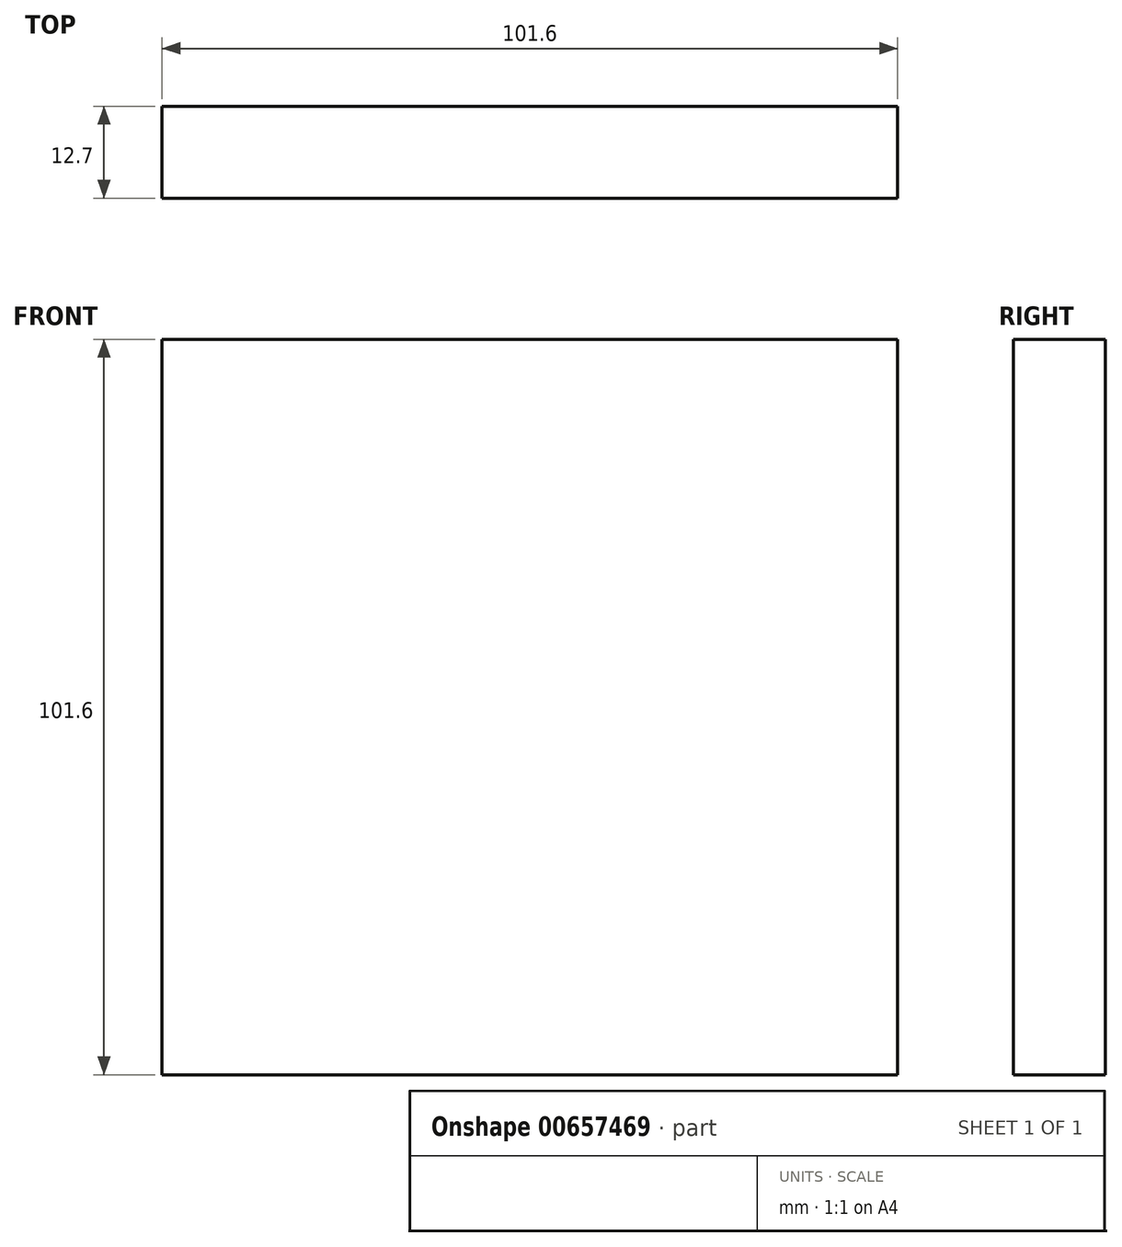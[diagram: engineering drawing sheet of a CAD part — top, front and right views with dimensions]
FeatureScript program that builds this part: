
annotation { "Feature Type Name" : "Feature", "Feature Type Description" : "" }
export const myFeature = defineFeature(function(context is Context, id is Id, definition is map)
    precondition{}
    {
        {
            var Q0;
            Q0=qCreatedBy(makeId("Front.planeOp"),FACE);
            var sketch = newSketch(context, id + "F0", { "sketchPlane" : qUnion([Q0])});
            skLineSegment(sketch, "E0.bottom", {"start": v(-47.38, 52.1) * mm, "end": v(54.22, 52.1) * mm});
            skLineSegment(sketch, "E0.top", {"start": v(-47.38, -49.5) * mm, "end": v(54.22, -49.5) * mm});
            skLineSegment(sketch, "E0.left", {"start": v(-47.38, 52.1) * mm, "end": v(-47.38, -49.5) * mm});
            skLineSegment(sketch, "E0.right", {"start": v(54.22, 52.1) * mm, "end": v(54.22, -49.5) * mm});
            skSolve(sketch);
        }
        {
            var Q0;
            Q0 = qSketchRegion(id + "F0", true);
            extrude(context, id + "F1", {"entities" : qUnion([Q0]), "depth" : 12.7 * mm, "offsetDistance" : 25.4 * mm});
        }
    });
